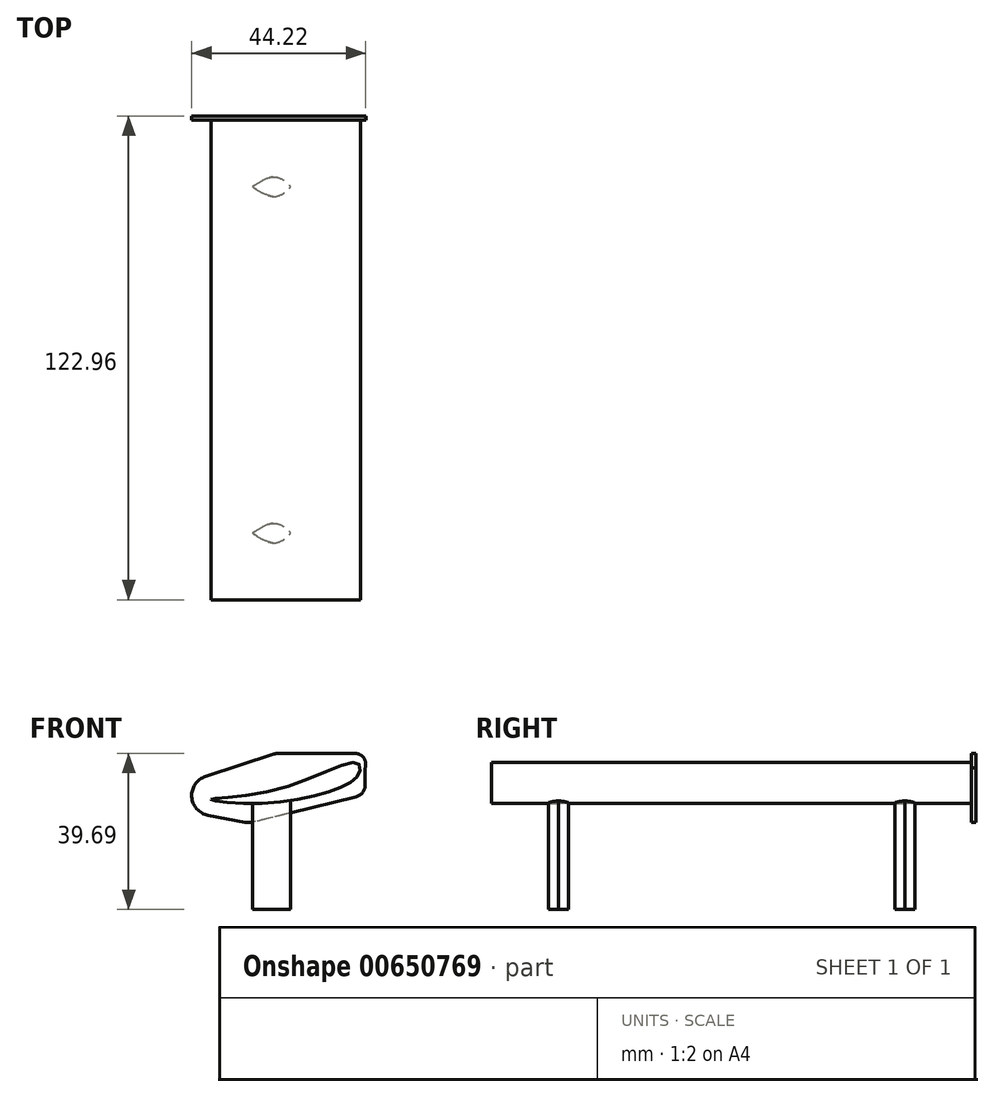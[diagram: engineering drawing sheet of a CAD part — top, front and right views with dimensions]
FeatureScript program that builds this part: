
annotation { "Feature Type Name" : "Feature", "Feature Type Description" : "" }
export const myFeature = defineFeature(function(context is Context, id is Id, definition is map)
    precondition{}
    {
        {
            var Q0;
            Q0=qCreatedBy(makeId("Front.planeOp"),FACE);
            var sketch = newSketch(context, id + "F0", { "sketchPlane" : qUnion([Q0])});
            skFitSpline(sketch, "E0", {"points": [v(0, 0) * mm, v(17.24, 2.62) * mm, v(37.15, 9.26) * mm, v(37.7, 6.68) * mm, v(32.36, 2.8) * mm, v(12.08, -1.07) * mm, v(0, 0) * mm]});
            skSolve(sketch);
        }
        {
            var Q0;
            Q0=makeQuery(id+"F0.imprint","IMPRINT",FACE,{"disambiguationData":[TD([[makeQuery(id+"F0.imprint","IMPRINT",EDGE,{"derivedFrom":sQuery(id+"F0.wireOp",EDGE,"E0")}),-1.0]])]});
            extrude(context, id + "F1", {"entities" : qUnion([Q0]), "depth" : 60.96 * mm, "offsetDistance" : 25.4 * mm, "hasSecondDirection" : true, "secondDirectionOppositeDirection" : true, "secondDirectionDepth" : 60.96 * mm});
        }
        {
            var Q0;
            Q0=qCreatedBy(makeId("Top.planeOp"),FACE);
            cPlane(context, id + "F2", {"entities" : qUnion([Q0]), "cplaneType" : CPlaneType.OFFSET, "offset" : 28 * mm, "oppositeDirection" : true, "width" : 152.4 * mm, "height" : 152.4 * mm});
        }
        {
            var Q0;
            Q0=qCreatedBy(id+"F2.planeOp",FACE);
            var sketch = newSketch(context, id + "F3", { "sketchPlane" : qUnion([Q0])});
            skFitSpline(sketch, "E1", {"points": [v(10.5, -44) * mm, v(15.8, -46.5) * mm], "startDerivative": vector(2.88, -1.85) * mm, "endDerivative": vector(6.09, -0.5) * mm});
            skFitSpline(sketch, "E2.MirrorCS", {"points": [v(10.5, -44) * mm, v(15.8, -41.5) * mm], "startDerivative": vector(2.88, 1.85) * mm, "endDerivative": vector(6.09, 0.5) * mm});
            skFitSpline(sketch, "E3", {"points": [v(20.2, -44) * mm, v(15.8, -46.5) * mm], "startDerivative": vector(-0.5, -0.95) * mm, "endDerivative": vector(-6.36, 0.52) * mm});
            skFitSpline(sketch, "E4.MirrorCS", {"points": [v(20.2, -44) * mm, v(15.8, -41.5) * mm], "startDerivative": vector(-0.5, 0.95) * mm, "endDerivative": vector(-6.36, -0.52) * mm});
            skFitSpline(sketch, "E5.MirrorCS", {"points": [v(20.2, 44) * mm, v(15.8, 46.5) * mm], "startDerivative": vector(-0.5, 0.95) * mm, "endDerivative": vector(-6.36, -0.52) * mm});
            skFitSpline(sketch, "E6.MirrorCS", {"points": [v(10.5, 44) * mm, v(15.8, 41.5) * mm], "startDerivative": vector(2.88, -1.85) * mm, "endDerivative": vector(6.09, -0.5) * mm});
            skFitSpline(sketch, "E7.MirrorCS", {"points": [v(10.5, 44) * mm, v(15.8, 46.5) * mm], "startDerivative": vector(2.88, 1.85) * mm, "endDerivative": vector(6.09, 0.5) * mm});
            skFitSpline(sketch, "E8.MirrorCS", {"points": [v(20.2, 44) * mm, v(15.8, 41.5) * mm], "startDerivative": vector(-0.5, -0.95) * mm, "endDerivative": vector(-6.36, 0.52) * mm});
            skSolve(sketch);
        }
        {
            var Q0;
            Q0 = qSketchRegion(id + "F3", true);
            extrude(context, id + "F4", {"entities" : qUnion([Q0]), "operationType" : NewBodyOperationType.ADD, "endBound" : BoundingType.UP_TO_NEXT, "depth" : 25 * mm, "offsetDistance" : 25 * mm});
        }
        {
            var Q0;
            Q0=qCreatedBy(makeId("Front.planeOp"),FACE);
            cPlane(context, id + "F5", {"entities" : qUnion([Q0]), "cplaneType" : CPlaneType.OFFSET, "offset" : 62 * mm, "oppositeDirection" : true, "width" : 150 * mm, "height" : 150 * mm});
        }
        {
            var Q0;
            Q0=qCreatedBy(id+"F5.planeOp",FACE);
            var sketch = newSketch(context, id + "F6", { "sketchPlane" : qUnion([Q0])});
            skLineSegment(sketch, "E9", {"start": v(16.02, 11.53) * mm, "end": v(-1.4, 5.82) * mm});
            skLineSegment(sketch, "E10", {"start": v(-0.75, -4.05) * mm, "end": v(9.76, -6) * mm});
            skLineSegment(sketch, "E11", {"start": v(36.87, 0.68) * mm, "end": v(9.76, -6) * mm});
            skArc(sketch, "E12", {"start": v(39.15, 8.02) * mm, "mid": v(38.8, 10.53) * mm, "end": v(36.55, 11.69) * mm});
            skArc(sketch, "E13", {"start": v(8.69, -5.8) * mm, "mid": v(9.76, -5.88) * mm, "end": v(10.83, -5.73) * mm});
            skLineSegment(sketch, "E14", {"start": v(17.01, 11.69) * mm, "end": v(36.55, 11.69) * mm});
            skLineSegment(sketch, "E15", {"start": v(39.15, 3.59) * mm, "end": v(39.15, 8.02) * mm});
            skArc(sketch, "E16", {"start": v(36.87, 0.68) * mm, "mid": v(38.51, 1.74) * mm, "end": v(39.15, 3.59) * mm});
            skPoint(sketch, "E17.orphan", {"position": v(20.28, -7.95) * mm});
            skPoint(sketch, "E18.center.orphan", {"position": v(17.86, 8.93) * mm});
            skArc(sketch, "E19", {"start": v(17.01, 11.69) * mm, "mid": v(16.5, 11.65) * mm, "end": v(16.02, 11.53) * mm});
            skPoint(sketch, "E20.center.orphan", {"position": v(1.13, 5.82) * mm});
            skArc(sketch, "E21", {"start": v(-1.4, 5.82) * mm, "mid": v(-4.9, 0.63) * mm, "end": v(-0.75, -4.05) * mm});
            skSolve(sketch);
        }
        {
            var Q0;
            Q0=makeQuery(id+"F6.imprint","IMPRINT",FACE,{"disambiguationData":[TD([[makeQuery(id+"F6.imprint","IMPRINT",EDGE,{"derivedFrom":sQuery(id+"F6.wireOp",EDGE,"E9")}),1.0]])]});
            var Q1;
            Q1=makeQuery(id+"F1.opExtrude","CAP_FACE",FACE,{"disambiguationData":[OSD([sQuery(id+"F0.wireOp",EDGE,"E0")])],"isStart":true});
            extrude(context, id + "F7", {"entities" : qUnion([Q0]), "operationType" : NewBodyOperationType.ADD, "endBound" : BoundingType.UP_TO_SURFACE, "depth" : 25 * mm, "endBoundEntityFace" : qUnion([Q1]), "offsetDistance" : 25 * mm});
        }
    });
